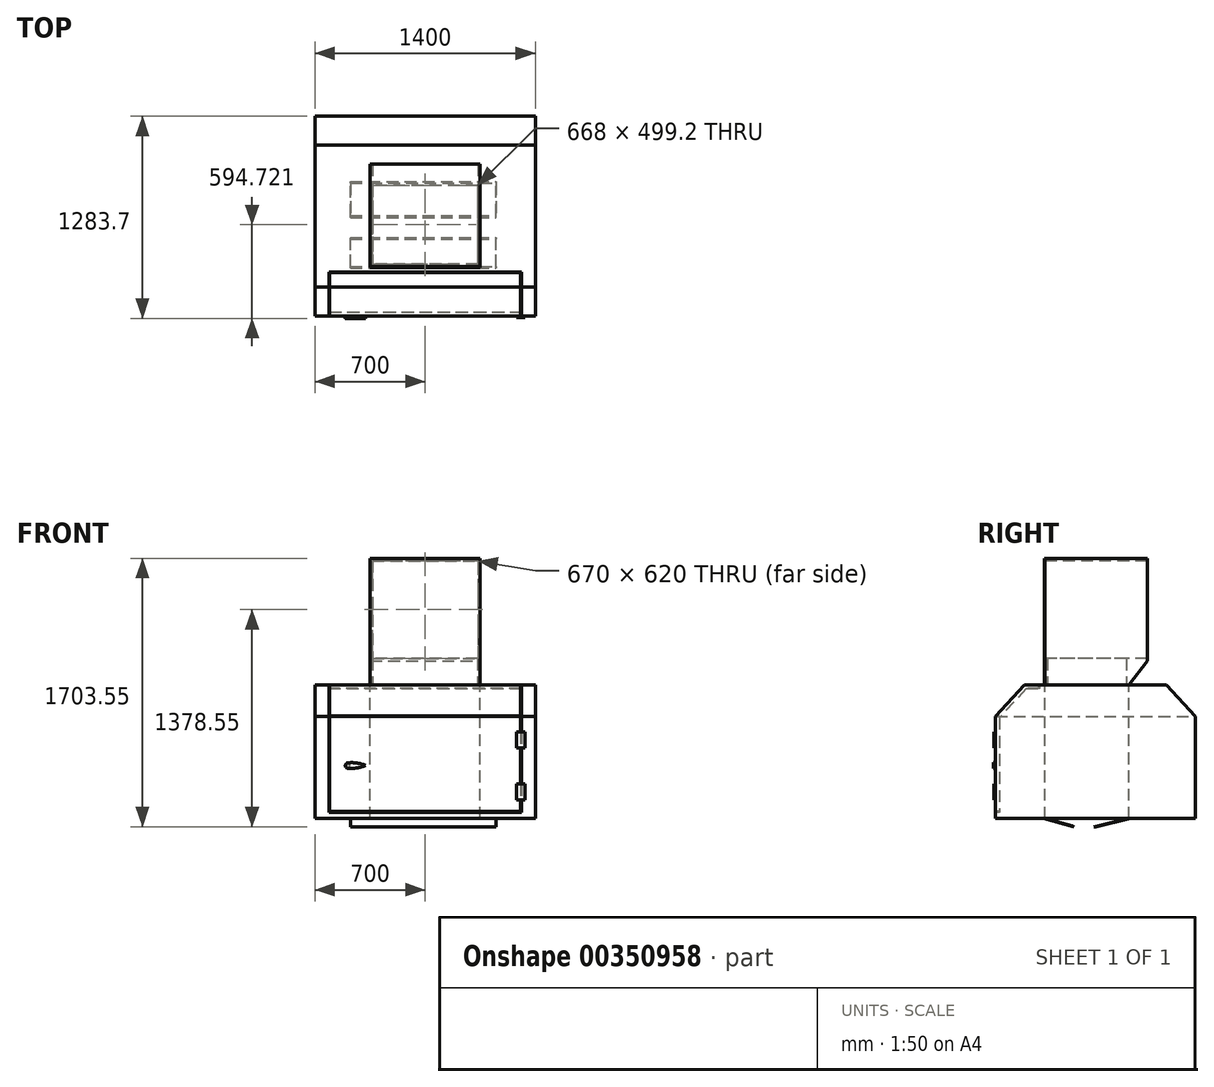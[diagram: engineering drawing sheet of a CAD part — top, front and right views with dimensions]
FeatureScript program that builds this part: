
annotation { "Feature Type Name" : "Feature", "Feature Type Description" : "" }
export const myFeature = defineFeature(function(context is Context, id is Id, definition is map)
    precondition{}
    {
        {
            var Q0;
            Q0=qCreatedBy(makeId("Front.planeOp"),FACE);
            var sketch = newSketch(context, id + "F0", { "sketchPlane" : qUnion([Q0])});
            skLineSegment(sketch, "E0.bottom", {"start": v(-335, 310) * mm, "end": v(335, 310) * mm});
            skLineSegment(sketch, "E0.top", {"start": v(-335, -310) * mm, "end": v(335, -310) * mm});
            skLineSegment(sketch, "E0.left", {"start": v(-335, 310) * mm, "end": v(-335, -310) * mm});
            skLineSegment(sketch, "E0.right", {"start": v(335, 310) * mm, "end": v(335, -310) * mm});
            skPoint(sketch, "E0.middle", {"position": v(0, 0) * mm});
            skLineSegment(sketch, "E1.bottom", {"start": v(-350, 325) * mm, "end": v(350, 325) * mm});
            skLineSegment(sketch, "E1.top", {"start": v(-350, -325) * mm, "end": v(350, -325) * mm});
            skLineSegment(sketch, "E1.left", {"start": v(-350, 325) * mm, "end": v(-350, -325) * mm});
            skLineSegment(sketch, "E1.right", {"start": v(350, 325) * mm, "end": v(350, -325) * mm});
            skSolve(sketch);
        }
        {
            var Q0;
            Q0 = qSketchRegion(id + "F0", true);
            extrude(context, id + "F1", {"entities" : qUnion([Q0]), "oppositeDirection" : true, "depth" : 650 * mm});
        }
        {
            var Q0;
            Q0=makeQuery(id+"F1.opExtrude","SWEPT_FACE",FACE,{"disambiguationData":[OSD([sQuery(id+"F0.wireOp",EDGE,"E1.right")])]});
            var sketch = newSketch(context, id + "F2", { "sketchPlane" : qUnion([Q0])});
            skLineSegment(sketch, "E2", {"start": v(650, -325) * mm, "end": v(0, -325) * mm});
            skLineSegment(sketch, "E3", {"start": v(650, -325) * mm, "end": v(531.2, -477.19) * mm});
            skLineSegment(sketch, "E4", {"start": v(0, -325) * mm, "end": v(0, -477.19) * mm});
            skLineSegment(sketch, "E5", {"start": v(0, -477.19) * mm, "end": v(531.2, -477.19) * mm});
            skSolve(sketch);
        }
        {
            var Q0;
            Q0=makeQuery(id+"F2.imprint","IMPRINT",FACE,{"disambiguationData":[TD([[makeQuery(id+"F2.imprint","IMPRINT",EDGE,{"derivedFrom":sQuery(id+"F2.wireOp",EDGE,"fvbqKa6w-FaTn-Zzt7-KS8a-4SE8wiSj7jWD")}),1.0]])]});
            var Q1;
            Q1=makeQuery(id+"F2.imprint","IMPRINT",FACE,{"disambiguationData":[TD([[makeQuery(id+"F2.imprint","IMPRINT",EDGE,{"derivedFrom":sQuery(id+"F2.wireOp",EDGE,"E2")}),1.0]])]});
            extrude(context, id + "F3", {"entities" : qUnion([Q0, Q1]), "operationType" : NewBodyOperationType.ADD, "oppositeDirection" : true, "depth" : 700 * mm});
        }
        {
            var Q0;
            Q0=makeQuery(id+"F3.opExtrude","SWEPT_FACE",FACE,{"disambiguationData":[OSD([sQuery(id+"F2.wireOp",EDGE,"E5")])]});
            var sketch = newSketch(context, id + "F4", { "sketchPlane" : qUnion([Q0])});
            skLineSegment(sketch, "E6.bottom", {"start": v(-700, 129.64) * mm, "end": v(700, 129.64) * mm});
            skLineSegment(sketch, "E6.top", {"start": v(-700, -770.36) * mm, "end": v(700, -770.36) * mm});
            skLineSegment(sketch, "E6.left", {"start": v(-700, 129.64) * mm, "end": v(-700, -770.36) * mm});
            skLineSegment(sketch, "E6.right", {"start": v(700, 129.64) * mm, "end": v(700, -770.36) * mm});
            skPoint(sketch, "E6.middle", {"position": v(0, -320.36) * mm});
            skPoint(sketch, "E6.middle.positionSnap0", {"position": v(-325, -320.36) * mm});
            skPoint(sketch, "E6.middle.positionSnap1", {"position": v(0, -650) * mm});
            skPoint(sketch, "E6.centerSnap0", {"position": v(-325, -320.36) * mm});
            skPoint(sketch, "E6.centerSnap1", {"position": v(0, -650) * mm});
            skSolve(sketch);
        }
        {
            var Q0;
            Q0=makeQuery(id+"F4.imprint","IMPRINT",FACE,{"disambiguationData":[TD([[makeQuery(id+"F4.imprint","IMPRINT",EDGE,{"derivedFrom":sQuery(id+"F4.wireOp",EDGE,"E6.bottom")}),-1.0]])]});
            extrude(context, id + "F5", {"entities" : qUnion([Q0]), "depth" : 200 * mm});
        }
        {
            var Q0;
            Q0=makeQuery(id+"F5.opExtrude","SWEPT_FACE",FACE,{"disambiguationData":[OSD([sQuery(id+"F4.wireOp",EDGE,"E6.right")])]});
            var sketch = newSketch(context, id + "F6", { "sketchPlane" : qUnion([Q0])});
            skLineSegment(sketch, "E7", {"start": v(-129.64, -477.19) * mm, "end": v(-313.99, -677.19) * mm});
            skLineSegment(sketch, "E8", {"start": v(-313.99, -677.19) * mm, "end": v(-129.64, -677.19) * mm});
            skLineSegment(sketch, "E9", {"start": v(320.36, -477.19) * mm, "end": v(320.36, -578.26) * mm});
            skLineSegment(sketch, "E10.MirrorCS", {"start": v(770.36, -477.19) * mm, "end": v(954.7, -677.19) * mm});
            skLineSegment(sketch, "E11.MirrorCS", {"start": v(954.7, -677.19) * mm, "end": v(770.36, -677.19) * mm});
            skSolve(sketch);
        }
        {
            var Q0;
            Q0 = qSketchRegion(id + "F6", true);
            var Q1;
            Q1=makeQuery(id+"F6.imprint","IMPRINT",FACE,{"disambiguationData":[TD([[makeQuery(id+"F6.imprint","IMPRINT",EDGE,{"derivedFrom":sQuery(id+"F6.wireOp",EDGE,"E7")}),1.0]])]});
            var Q2;
            Q2=makeQuery(id+"F6.imprint","IMPRINT",FACE,{"disambiguationData":[TD([[makeQuery(id+"F6.imprint","IMPRINT",EDGE,{"derivedFrom":sQuery(id+"F6.wireOp",EDGE,"E10.MirrorCS")}),-1.0]])]});
            extrude(context, id + "F7", {"entities" : qUnion([Q0, Q1, Q2]), "operationType" : NewBodyOperationType.ADD, "oppositeDirection" : true, "depth" : 1400 * mm});
        }
        {
            var Q0;
            Q0=makeQuery(id+"F7.boolean.opBoolean","MERGE",FACE,{"derivedFrom":[makeQuery(id+"F5.opExtrude","CAP_FACE",FACE,{"disambiguationData":[OSD([sQuery(id+"F2.wireOp",EDGE,"E3"),sQuery(id+"F2.wireOp",EDGE,"E4"),sQuery(id+"F2.wireOp",EDGE,"E5"),sQuery(id+"F4.wireOp",EDGE,"E6.bottom"),sQuery(id+"F4.wireOp",EDGE,"E6.top"),sQuery(id+"F4.wireOp",EDGE,"E6.left"),sQuery(id+"F4.wireOp",EDGE,"E6.right")])],"isStart":false}),makeQuery(id+"F7.opExtrude","SWEPT_FACE",FACE,{"disambiguationData":[OSD([sQuery(id+"F6.wireOp",EDGE,"E8")])]}),makeQuery(id+"F7.opExtrude","SWEPT_FACE",FACE,{"disambiguationData":[OSD([sQuery(id+"F6.wireOp",EDGE,"E11.MirrorCS")])]})]});
            var sketch = newSketch(context, id + "F8", { "sketchPlane" : qUnion([Q0])});
            skLineSegment(sketch, "E12.bottom", {"start": v(700, 313.99) * mm, "end": v(-699.8, 313.99) * mm});
            skLineSegment(sketch, "E12.top", {"start": v(700, -954.7) * mm, "end": v(-699.8, -954.7) * mm});
            skLineSegment(sketch, "E12.left", {"start": v(700, 313.99) * mm, "end": v(700, -954.7) * mm});
            skLineSegment(sketch, "E12.right", {"start": v(-699.8, 313.99) * mm, "end": v(-699.8, -954.7) * mm});
            skPoint(sketch, "E12.middle", {"position": v(0.1, -320.36) * mm});
            skPoint(sketch, "E12.middle.positionSnap0", {"position": v(0.1, -54.76) * mm});
            skPoint(sketch, "E12.middle.positionSnap1", {"position": v(700, -320.36) * mm});
            skPoint(sketch, "E12.centerSnap0", {"position": v(0.1, -54.76) * mm});
            skPoint(sketch, "E12.centerSnap1", {"position": v(700, -320.36) * mm});
            skSolve(sketch);
        }
        {
            var Q0;
            Q0=makeQuery(id+"F8.imprint","IMPRINT",FACE,{"disambiguationData":[TD([[makeQuery(id+"F8.imprint","IMPRINT",EDGE,{"derivedFrom":sQuery(id+"F8.wireOp",EDGE,"E12.bottom")}),-1.0]])]});
            extrude(context, id + "F9", {"entities" : qUnion([Q0]), "operationType" : NewBodyOperationType.ADD, "depth" : 650 * mm});
        }
        {
            var Q0;
            Q0=makeQuery(id+"F9.opExtrude","SWEPT_FACE",FACE,{"disambiguationData":[OSD([sQuery(id+"F8.wireOp",EDGE,"E12.bottom")])]});
            var sketch = newSketch(context, id + "F10", { "sketchPlane" : qUnion([Q0])});
            skLineSegment(sketch, "E13.bottom", {"start": v(-611.32, -676.78) * mm, "end": v(611.53, -676.78) * mm});
            skLineSegment(sketch, "E13.top", {"start": v(-611.32, -1327.6) * mm, "end": v(611.53, -1327.6) * mm});
            skLineSegment(sketch, "E13.left", {"start": v(-611.32, -676.78) * mm, "end": v(-611.32, -1327.6) * mm});
            skLineSegment(sketch, "E13.right", {"start": v(611.53, -676.78) * mm, "end": v(611.53, -1327.6) * mm});
            skPoint(sketch, "E13.middle", {"position": v(0.1, -1002.19) * mm});
            skPoint(sketch, "E13.middle.positionSnap0", {"position": v(-699.8, -1002.19) * mm});
            skPoint(sketch, "E13.middle.positionSnap1", {"position": v(0.1, -677.19) * mm});
            skPoint(sketch, "E13.centerSnap0", {"position": v(-699.8, -1002.19) * mm});
            skPoint(sketch, "E13.centerSnap1", {"position": v(0.1, -677.19) * mm});
            skLineSegment(sketch, "E14", {"start": v(-611.32, -1286.62) * mm, "end": v(611.53, -1286.62) * mm});
            skLineSegment(sketch, "E15", {"start": v(-606.32, -677.19) * mm, "end": v(-606.32, -1286.62) * mm});
            skLineSegment(sketch, "E16", {"start": v(606.53, -677.19) * mm, "end": v(606.53, -1286.62) * mm});
            skLineSegment(sketch, "E17", {"start": v(-606.32, -1281.62) * mm, "end": v(606.53, -1281.62) * mm});
            skSolve(sketch);
        }
        {
            var Q0;
            {var subQ0=sQuery(id+"F10.wireOp",EDGE,"E13.top");Q0=makeQuery(id+"F10.imprint","IMPRINT",FACE,{"disambiguationData":[TD([[makeQuery(id+"F10.imprint","IMPRINT",EDGE,{"derivedFrom":subQ0}),1.0]])]});}
            var Q1;
            {var subQ5=sQuery(id+"F10.wireOp",EDGE,"E15");Q1=makeQuery(id+"F10.imprint","IMPRINT",FACE,{"disambiguationData":[TD([[makeQuery(id+"F10.imprint","IMPRINT",EDGE,{"derivedFrom":subQ5}),-1.0]])]});}
            var Q2;
            {var subQ5=sQuery(id+"F10.wireOp",EDGE,"E16");Q2=makeQuery(id+"F10.imprint","IMPRINT",FACE,{"disambiguationData":[TD([[makeQuery(id+"F10.imprint","IMPRINT",EDGE,{"derivedFrom":subQ5}),1.0]])]});}
            var Q3;
            {var subQ1=sQuery(id+"F10.wireOp",EDGE,"E13.bottom");Q3=makeQuery(id+"F10.imprint","IMPRINT",FACE,{"disambiguationData":[TD([[makeQuery(id+"F10.imprint","IMPRINT",EDGE,{"derivedFrom":subQ1}),-1.0]])]});}
            var Q4;
            {var subQ5=sQuery(id+"F10.wireOp",EDGE,"E17");Q4=makeQuery(id+"F10.imprint","IMPRINT",FACE,{"disambiguationData":[TD([[makeQuery(id+"F10.imprint","IMPRINT",EDGE,{"derivedFrom":subQ5}),-1.0]])]});}
            extrude(context, id + "F11", {"entities" : qUnion([Q0, Q1, Q2, Q3, Q4]), "operationType" : NewBodyOperationType.REMOVE, "oppositeDirection" : true, "depth" : 25 * mm});
        }
        {
            var Q0;
            Q0=makeQuery(id+"F7.opExtrude","SWEPT_FACE",FACE,{"disambiguationData":[OSD([sQuery(id+"F6.wireOp",EDGE,"E7")])]});
            var sketch = newSketch(context, id + "F12", { "sketchPlane" : qUnion([Q0])});
            skLineSegment(sketch, "E18", {"start": v(-611.32, -710.18) * mm, "end": v(-611.32, -438.73) * mm});
            skLineSegment(sketch, "E19", {"start": v(-611.32, -438.73) * mm, "end": v(-606.32, -438.73) * mm});
            skLineSegment(sketch, "E20", {"start": v(-606.32, -438.73) * mm, "end": v(-606.32, -710.18) * mm});
            skLineSegment(sketch, "E21", {"start": v(-611.32, -710.18) * mm, "end": v(-606.32, -710.18) * mm});
            skLineSegment(sketch, "E22", {"start": v(611.53, -710.18) * mm, "end": v(611.53, -438.73) * mm});
            skLineSegment(sketch, "E23", {"start": v(611.53, -438.73) * mm, "end": v(606.53, -438.73) * mm});
            skLineSegment(sketch, "E24", {"start": v(606.53, -438.73) * mm, "end": v(606.53, -710.18) * mm});
            skLineSegment(sketch, "E25", {"start": v(606.53, -710.18) * mm, "end": v(611.53, -710.18) * mm});
            skSolve(sketch);
        }
        {
            var Q0;
            Q0=makeQuery(id+"F12.imprint","IMPRINT",FACE,{"disambiguationData":[TD([[makeQuery(id+"F12.imprint","IMPRINT",EDGE,{"derivedFrom":sQuery(id+"F12.wireOp",EDGE,"E22")}),1.0]])]});
            var Q1;
            Q1=makeQuery(id+"F12.imprint","IMPRINT",FACE,{"disambiguationData":[TD([[makeQuery(id+"F12.imprint","IMPRINT",EDGE,{"derivedFrom":sQuery(id+"F12.wireOp",EDGE,"E18")}),-1.0]])]});
            extrude(context, id + "F13", {"entities" : qUnion([Q0, Q1]), "operationType" : NewBodyOperationType.REMOVE, "oppositeDirection" : true, "depth" : 25 * mm});
        }
        {
            var Q0;
            Q0=makeQuery(id+"F5.opExtrude","CAP_FACE",FACE,{"disambiguationData":[OSD([sQuery(id+"F2.wireOp",EDGE,"fvbqKa6w-FaTn-Zzt7-KS8a-4SE8wiSj7jWD"),sQuery(id+"F2.wireOp",EDGE,"2xf041MG-nKwf-17Tv-A2xk-tNd3sgYRvjPP"),sQuery(id+"F2.wireOp",EDGE,"aVLETtaD-QBmV-cSdN-3RXo-Neing0HmeXMZ"),sQuery(id+"F4.wireOp",EDGE,"E6.bottom"),sQuery(id+"F4.wireOp",EDGE,"E6.top"),sQuery(id+"F4.wireOp",EDGE,"E6.left"),sQuery(id+"F4.wireOp",EDGE,"E6.right")])],"isStart":true});
            var sketch = newSketch(context, id + "F14", { "sketchPlane" : qUnion([Q0])});
            skLineSegment(sketch, "E26", {"start": v(-611.32, -33.9) * mm, "end": v(611.53, -33.9) * mm});
            skLineSegment(sketch, "E27", {"start": v(611.53, -33.9) * mm, "end": v(611.53, -129.64) * mm});
            skLineSegment(sketch, "E28", {"start": v(606.53, -129.64) * mm, "end": v(606.53, -38.9) * mm});
            skLineSegment(sketch, "E29", {"start": v(606.53, -38.9) * mm, "end": v(-606.32, -38.9) * mm});
            skLineSegment(sketch, "E30", {"start": v(-611.32, -33.9) * mm, "end": v(-611.32, -129.64) * mm});
            skLineSegment(sketch, "E31", {"start": v(-606.32, -129.64) * mm, "end": v(-606.32, -38.9) * mm});
            skSolve(sketch);
        }
        {
            var Q0;
            Q0 = qSketchRegion(id + "F14", true);
            var Q1;
            Q1=makeQuery(id+"F14.imprint","IMPRINT",FACE,{"disambiguationData":[TD([[makeQuery(id+"F14.imprint","IMPRINT",EDGE,{"derivedFrom":sQuery(id+"F14.wireOp",EDGE,"E26")}),-1.0]])]});
            extrude(context, id + "F15", {"entities" : qUnion([Q0, Q1]), "operationType" : NewBodyOperationType.REMOVE, "oppositeDirection" : true, "depth" : 25 * mm});
        }
        {
            var Q0;
            {var subQ0=sQuery(id+"F8.wireOp",EDGE,"E12.bottom");Q0=makeQuery(id+"F11.boolean.opBoolean","SPLIT",FACE,{"disambiguationData":[TD([makeQuery(id+"F11.opExtrude","SWEPT_FACE",FACE,{"disambiguationData":[OSD([sQuery(id+"F10.wireOp",EDGE,"E15")])]})])],"derivedFrom":makeQuery(id+"F9.opExtrude","SWEPT_FACE",FACE,{"disambiguationData":[OSD([subQ0])]})});}
            var sketch = newSketch(context, id + "F16", { "sketchPlane" : qUnion([Q0])});
            skLineSegment(sketch, "E32.bottom", {"start": v(580, -1108.2) * mm, "end": v(635, -1108.2) * mm});
            skLineSegment(sketch, "E32.top", {"start": v(580, -1208.2) * mm, "end": v(635, -1208.2) * mm});
            skLineSegment(sketch, "E32.left", {"start": v(580, -1108.2) * mm, "end": v(580, -1208.2) * mm});
            skLineSegment(sketch, "E32.right", {"start": v(635, -1108.2) * mm, "end": v(635, -1208.2) * mm});
            skLineSegment(sketch, "E33.bottom", {"start": v(580, -777.19) * mm, "end": v(635, -777.19) * mm});
            skLineSegment(sketch, "E33.top", {"start": v(580, -877.19) * mm, "end": v(635, -877.19) * mm});
            skLineSegment(sketch, "E33.left", {"start": v(580, -777.19) * mm, "end": v(580, -877.19) * mm});
            skLineSegment(sketch, "E33.right", {"start": v(635, -777.19) * mm, "end": v(635, -877.19) * mm});
            skLineSegment(sketch, "E34", {"start": v(635, -808.1) * mm, "end": v(700, -808.1) * mm});
            skLineSegment(sketch, "E35", {"start": v(635, -1168.82) * mm, "end": v(700, -1168.82) * mm});
            skCircle(sketch, "E36", {"center": v(-489.5, -990.94) * mm, "radius": 11.33 * mm});
            skSolve(sketch);
        }
        {
            var Q0;
            Q0 = qSketchRegion(id + "F16", true);
            extrude(context, id + "F17", {"entities" : qUnion([Q0]), "operationType" : NewBodyOperationType.ADD, "depth" : 5 * mm});
        }
        {
            var Q0;
            Q0 = qSketchRegion(id + "F16", true);
            extrude(context, id + "F18", {"entities" : qUnion([Q0]), "operationType" : NewBodyOperationType.ADD, "depth" : 10 * mm});
        }
        {
            var Q0;
            Q0=makeQuery(id+"F18.opExtrude","CAP_FACE",FACE,{"disambiguationData":[OSD([sQuery(id+"F16.wireOp",EDGE,"E36")])],"isStart":false});
            var sketch = newSketch(context, id + "F19", { "sketchPlane" : qUnion([Q0])});
            skCircle(sketch, "E37", {"center": v(-489.5, -990.94) * mm, "radius": 17.59 * mm});
            skArc(sketch, "E38", {"start": v(-378.58, -989.39) * mm, "mid": v(-433.72, -974.28) * mm, "end": v(-490.88, -973.4) * mm});
            skArc(sketch, "E39", {"start": v(-489.5, -1008.53) * mm, "mid": v(-432.84, -1005.92) * mm, "end": v(-378.58, -989.39) * mm});
            skSolve(sketch);
        }
        {
            var Q0;
            Q0 = qSketchRegion(id + "F19", true);
            extrude(context, id + "F20", {"entities" : qUnion([Q0]), "operationType" : NewBodyOperationType.ADD, "depth" : 5 * mm});
        }
        {
            var Q0;
            Q0=makeQuery(id+"F3.opExtrude","SWEPT_FACE",FACE,{"disambiguationData":[OSD([sQuery(id+"F2.wireOp",EDGE,"E5")])]});
            var sketch = newSketch(context, id + "F21", { "sketchPlane" : qUnion([Q0])});
            skLineSegment(sketch, "E40.bottom", {"start": v(-350, -0.13) * mm, "end": v(350, -0.13) * mm});
            skLineSegment(sketch, "E40.top", {"start": v(-350, -531.33) * mm, "end": v(350, -531.33) * mm});
            skLineSegment(sketch, "E40.left", {"start": v(-350, -0.13) * mm, "end": v(-350, -531.33) * mm});
            skLineSegment(sketch, "E40.right", {"start": v(350, -0.13) * mm, "end": v(350, -531.33) * mm});
            skLineSegment(sketch, "E41.bottom", {"start": v(334, -515.33) * mm, "end": v(-334, -515.33) * mm});
            skLineSegment(sketch, "E41.top", {"start": v(334, -16.13) * mm, "end": v(-334, -16.13) * mm});
            skLineSegment(sketch, "E41.left", {"start": v(334, -515.33) * mm, "end": v(334, -16.13) * mm});
            skLineSegment(sketch, "E41.right", {"start": v(-334, -515.33) * mm, "end": v(-334, -16.13) * mm});
            skSolve(sketch);
        }
        {
            var Q0;
            Q0=makeQuery(id+"F21.imprint","IMPRINT",FACE,{"disambiguationData":[TD([[makeQuery(id+"F21.imprint","IMPRINT",EDGE,{"derivedFrom":sQuery(id+"F21.wireOp",EDGE,"E41.bottom")}),-1.0]])]});
            extrude(context, id + "F22", {"entities" : qUnion([Q0]), "operationType" : NewBodyOperationType.REMOVE, "oppositeDirection" : true, "depth" : 170 * mm});
        }
        {
            var Q0;
            Q0=makeQuery(id+"F3.boolean.opBoolean","MERGE",FACE,{"derivedFrom":[makeQuery(id+"F1.opExtrude","CAP_FACE",FACE,{"disambiguationData":[OSD([sQuery(id+"F0.wireOp",EDGE,"E0.bottom"),sQuery(id+"F0.wireOp",EDGE,"E0.top"),sQuery(id+"F0.wireOp",EDGE,"E0.left"),sQuery(id+"F0.wireOp",EDGE,"E0.right"),sQuery(id+"F0.wireOp",EDGE,"E1.bottom"),sQuery(id+"F0.wireOp",EDGE,"E1.top"),sQuery(id+"F0.wireOp",EDGE,"E1.left"),sQuery(id+"F0.wireOp",EDGE,"E1.right")])],"isStart":true}),makeQuery(id+"F3.opExtrude","SWEPT_FACE",FACE,{"disambiguationData":[OSD([sQuery(id+"F2.wireOp",EDGE,"E4")])]})]});
            var sketch = newSketch(context, id + "F23", { "sketchPlane" : qUnion([Q0])});
            skLineSegment(sketch, "E42.bottom", {"start": v(-350, 325) * mm, "end": v(350, 325) * mm});
            skLineSegment(sketch, "E42.top", {"start": v(-350, -477.19) * mm, "end": v(350, -477.19) * mm});
            skLineSegment(sketch, "E42.left", {"start": v(-350, 325) * mm, "end": v(-350, -477.19) * mm});
            skLineSegment(sketch, "E42.right", {"start": v(350, 325) * mm, "end": v(350, -477.19) * mm});
            skSolve(sketch);
        }
        {
            var Q0;
            Q0 = qSketchRegion(id + "F23", true);
            extrude(context, id + "F24", {"entities" : qUnion([Q0]), "depth" : 5 * mm});
        }
        {
            var Q0;
            {var subQ0=sQuery(id+"F4.wireOp",EDGE,"E6.right");Q0=makeQuery(id+"F9.boolean.opBoolean","MERGE",FACE,{"derivedFrom":[makeQuery(id+"F7.boolean.opBoolean","MERGE",FACE,{"derivedFrom":[makeQuery(id+"F5.opExtrude","SWEPT_FACE",FACE,{"disambiguationData":[OSD([subQ0])]}),makeQuery(id+"F7.opExtrude","CAP_FACE",FACE,{"disambiguationData":[OSD([sQuery(id+"F4.wireOp",EDGE,"E6.bottom"),subQ0,sQuery(id+"F6.wireOp",EDGE,"E7"),sQuery(id+"F6.wireOp",EDGE,"E8")])],"isStart":true}),makeQuery(id+"F7.opExtrude","CAP_FACE",FACE,{"disambiguationData":[OSD([sQuery(id+"F4.wireOp",EDGE,"E6.top"),subQ0,sQuery(id+"F6.wireOp",EDGE,"E10.MirrorCS"),sQuery(id+"F6.wireOp",EDGE,"E11.MirrorCS")])],"isStart":true})]}),makeQuery(id+"F9.opExtrude","SWEPT_FACE",FACE,{"disambiguationData":[OSD([sQuery(id+"F8.wireOp",EDGE,"E12.left")])]})]});}
            var sketch = newSketch(context, id + "F25", { "sketchPlane" : qUnion([Q0])});
            skLineSegment(sketch, "E43", {"start": v(0, -1327.19) * mm, "end": v(173.96, -1373.41) * mm});
            skLineSegment(sketch, "E44", {"start": v(530, -1327.19) * mm, "end": v(311.43, -1378.55) * mm});
            skLineSegment(sketch, "E45", {"start": v(-9.54, -1327.19) * mm, "end": v(183.75, -1378.55) * mm});
            skLineSegment(sketch, "E46", {"start": v(322.48, -1378.55) * mm, "end": v(541.05, -1327.19) * mm});
            skLineSegment(sketch, "E47", {"start": v(183.75, -1378.55) * mm, "end": v(173.96, -1373.41) * mm});
            skLineSegment(sketch, "E48", {"start": v(311.43, -1378.55) * mm, "end": v(322.48, -1378.55) * mm});
            skSolve(sketch);
        }
        {
            var Q0;
            {var subQ0=sQuery(id+"F25.wireOp",EDGE,"E43");Q0=makeQuery(id+"F25.imprint","IMPRINT",FACE,{"disambiguationData":[TD([[makeQuery(id+"F25.imprint","IMPRINT",EDGE,{"derivedFrom":subQ0}),-1.0]])]});}
            var Q1;
            {var subQ0=sQuery(id+"F25.wireOp",EDGE,"E44");Q1=makeQuery(id+"F25.imprint","IMPRINT",FACE,{"disambiguationData":[TD([[makeQuery(id+"F25.imprint","IMPRINT",EDGE,{"derivedFrom":subQ0}),1.0]])]});}
            extrude(context, id + "F26", {"entities" : qUnion([Q0, Q1]), "operationType" : NewBodyOperationType.ADD, "oppositeDirection" : true, "depth" : 1175 * mm});
        }
        {
            var Q0;
            {var subQ0=sQuery(id+"F8.wireOp",EDGE,"E12.left");var subQ1=sQuery(id+"F4.wireOp",EDGE,"E6.right");Q0=makeQuery(id+"F26.boolean.opBoolean","MERGE",FACE,{"derivedFrom":[makeQuery(id+"F9.boolean.opBoolean","MERGE",FACE,{"derivedFrom":[makeQuery(id+"F7.boolean.opBoolean","MERGE",FACE,{"derivedFrom":[makeQuery(id+"F5.opExtrude","SWEPT_FACE",FACE,{"disambiguationData":[OSD([subQ1])]}),makeQuery(id+"F7.opExtrude","CAP_FACE",FACE,{"disambiguationData":[OSD([sQuery(id+"F4.wireOp",EDGE,"E6.bottom"),subQ1,sQuery(id+"F6.wireOp",EDGE,"E7"),sQuery(id+"F6.wireOp",EDGE,"E8")])],"isStart":true}),makeQuery(id+"F7.opExtrude","CAP_FACE",FACE,{"disambiguationData":[OSD([sQuery(id+"F4.wireOp",EDGE,"E6.top"),subQ1,sQuery(id+"F6.wireOp",EDGE,"E10.MirrorCS"),sQuery(id+"F6.wireOp",EDGE,"E11.MirrorCS")])],"isStart":true})]}),makeQuery(id+"F9.opExtrude","SWEPT_FACE",FACE,{"disambiguationData":[OSD([subQ0])]})]}),makeQuery(id+"F26.opExtrude","CAP_FACE",FACE,{"disambiguationData":[OSD([subQ0,sQuery(id+"F25.wireOp",EDGE,"E43"),sQuery(id+"F25.wireOp",EDGE,"E45"),sQuery(id+"F25.wireOp",EDGE,"E47")])],"isStart":true}),makeQuery(id+"F26.opExtrude","CAP_FACE",FACE,{"disambiguationData":[OSD([subQ0,sQuery(id+"F25.wireOp",EDGE,"E44"),sQuery(id+"F25.wireOp",EDGE,"E46"),sQuery(id+"F25.wireOp",EDGE,"E48")])],"isStart":true})]});}
            var sketch = newSketch(context, id + "F27", { "sketchPlane" : qUnion([Q0])});
            skLineSegment(sketch, "E49", {"start": v(183.75, -1378.55) * mm, "end": v(173.96, -1373.41) * mm});
            skLineSegment(sketch, "E50", {"start": v(173.96, -1373.41) * mm, "end": v(0, -1327.19) * mm});
            skLineSegment(sketch, "E51", {"start": v(0, -1327.19) * mm, "end": v(-9.54, -1327.19) * mm});
            skLineSegment(sketch, "E52", {"start": v(-9.54, -1327.19) * mm, "end": v(183.75, -1378.55) * mm});
            skSolve(sketch);
        }
        {
            var Q0;
            Q0=makeQuery(id+"F27.imprint","IMPRINT",FACE,{"disambiguationData":[TD([[makeQuery(id+"F27.imprint","IMPRINT",EDGE,{"derivedFrom":sQuery(id+"F27.wireOp",EDGE,"E49")}),1.0]])]});
            extrude(context, id + "F28", {"entities" : qUnion([Q0]), "operationType" : NewBodyOperationType.REMOVE, "oppositeDirection" : true, "depth" : 250 * mm});
        }
        {
            var Q0;
            {var subQ0=sQuery(id+"F8.wireOp",EDGE,"E12.left");var subQ1=sQuery(id+"F4.wireOp",EDGE,"E6.right");Q0=makeQuery(id+"F26.boolean.opBoolean","MERGE",FACE,{"derivedFrom":[makeQuery(id+"F9.boolean.opBoolean","MERGE",FACE,{"derivedFrom":[makeQuery(id+"F7.boolean.opBoolean","MERGE",FACE,{"derivedFrom":[makeQuery(id+"F5.opExtrude","SWEPT_FACE",FACE,{"disambiguationData":[OSD([subQ1])]}),makeQuery(id+"F7.opExtrude","CAP_FACE",FACE,{"disambiguationData":[OSD([sQuery(id+"F4.wireOp",EDGE,"E6.bottom"),subQ1,sQuery(id+"F6.wireOp",EDGE,"E7"),sQuery(id+"F6.wireOp",EDGE,"E8")])],"isStart":true}),makeQuery(id+"F7.opExtrude","CAP_FACE",FACE,{"disambiguationData":[OSD([sQuery(id+"F4.wireOp",EDGE,"E6.top"),subQ1,sQuery(id+"F6.wireOp",EDGE,"E10.MirrorCS"),sQuery(id+"F6.wireOp",EDGE,"E11.MirrorCS")])],"isStart":true})]}),makeQuery(id+"F9.opExtrude","SWEPT_FACE",FACE,{"disambiguationData":[OSD([subQ0])]})]}),makeQuery(id+"F26.opExtrude","CAP_FACE",FACE,{"disambiguationData":[OSD([subQ0,sQuery(id+"F25.wireOp",EDGE,"E43"),sQuery(id+"F25.wireOp",EDGE,"E45"),sQuery(id+"F25.wireOp",EDGE,"E47")])],"isStart":true}),makeQuery(id+"F26.opExtrude","CAP_FACE",FACE,{"disambiguationData":[OSD([subQ0,sQuery(id+"F25.wireOp",EDGE,"E44"),sQuery(id+"F25.wireOp",EDGE,"E46"),sQuery(id+"F25.wireOp",EDGE,"E48")])],"isStart":true})]});}
            var sketch = newSketch(context, id + "F29", { "sketchPlane" : qUnion([Q0])});
            skLineSegment(sketch, "E53", {"start": v(311.43, -1378.55) * mm, "end": v(322.48, -1378.55) * mm});
            skLineSegment(sketch, "E54", {"start": v(322.48, -1378.55) * mm, "end": v(541.05, -1327.19) * mm});
            skLineSegment(sketch, "E55", {"start": v(541.05, -1327.19) * mm, "end": v(530, -1327.19) * mm});
            skLineSegment(sketch, "E56", {"start": v(530, -1327.19) * mm, "end": v(311.43, -1378.55) * mm});
            skSolve(sketch);
        }
        {
            var Q0;
            Q0=makeQuery(id+"F29.imprint","IMPRINT",FACE,{"disambiguationData":[TD([[makeQuery(id+"F29.imprint","IMPRINT",EDGE,{"derivedFrom":sQuery(id+"F29.wireOp",EDGE,"E53")}),1.0]])]});
            extrude(context, id + "F30", {"entities" : qUnion([Q0]), "operationType" : NewBodyOperationType.REMOVE, "oppositeDirection" : true, "depth" : 250 * mm});
        }
    });
